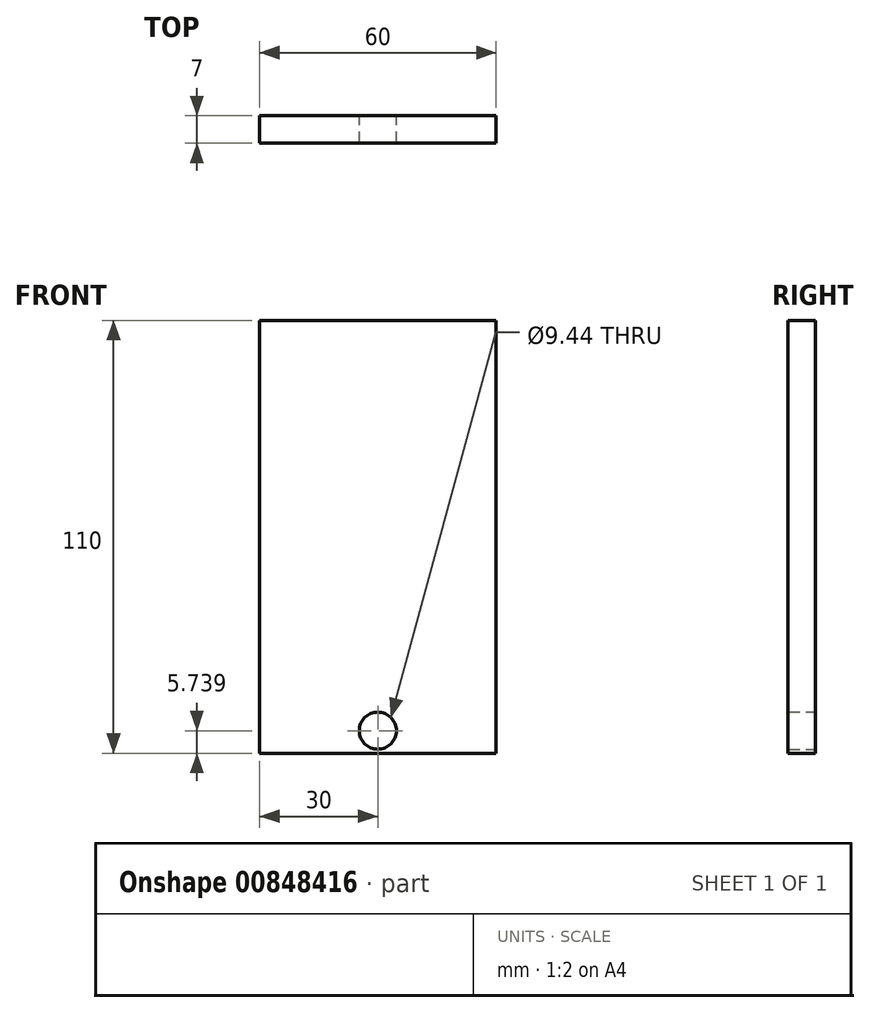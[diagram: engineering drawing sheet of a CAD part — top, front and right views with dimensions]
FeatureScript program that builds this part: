
annotation { "Feature Type Name" : "Feature", "Feature Type Description" : "" }
export const myFeature = defineFeature(function(context is Context, id is Id, definition is map)
    precondition{}
    {
        {
            var Q0;
            Q0=qCreatedBy(makeId("Front.planeOp"),FACE);
            var sketch = newSketch(context, id + "F0", { "sketchPlane" : qUnion([Q0])});
            skLineSegment(sketch, "E0.bottom", {"start": v(-30, 55) * mm, "end": v(30, 55) * mm});
            skLineSegment(sketch, "E0.top", {"start": v(-30, -55) * mm, "end": v(30, -55) * mm});
            skLineSegment(sketch, "E0.left", {"start": v(-30, 55) * mm, "end": v(-30, -55) * mm});
            skLineSegment(sketch, "E0.right", {"start": v(30, 55) * mm, "end": v(30, -55) * mm});
            skPoint(sketch, "E0.middle", {"position": v(0, 0) * mm});
            skCircle(sketch, "E1", {"center": v(0, -49.26) * mm, "radius": 4.72 * mm});
            skSolve(sketch);
        }
        {
            var Q0;
            Q0 = qSketchRegion(id + "F0", true);
            extrude(context, id + "F1", {"entities" : qUnion([Q0]), "depth" : 7 * mm, "offsetDistance" : 25.4 * mm});
        }
    });
